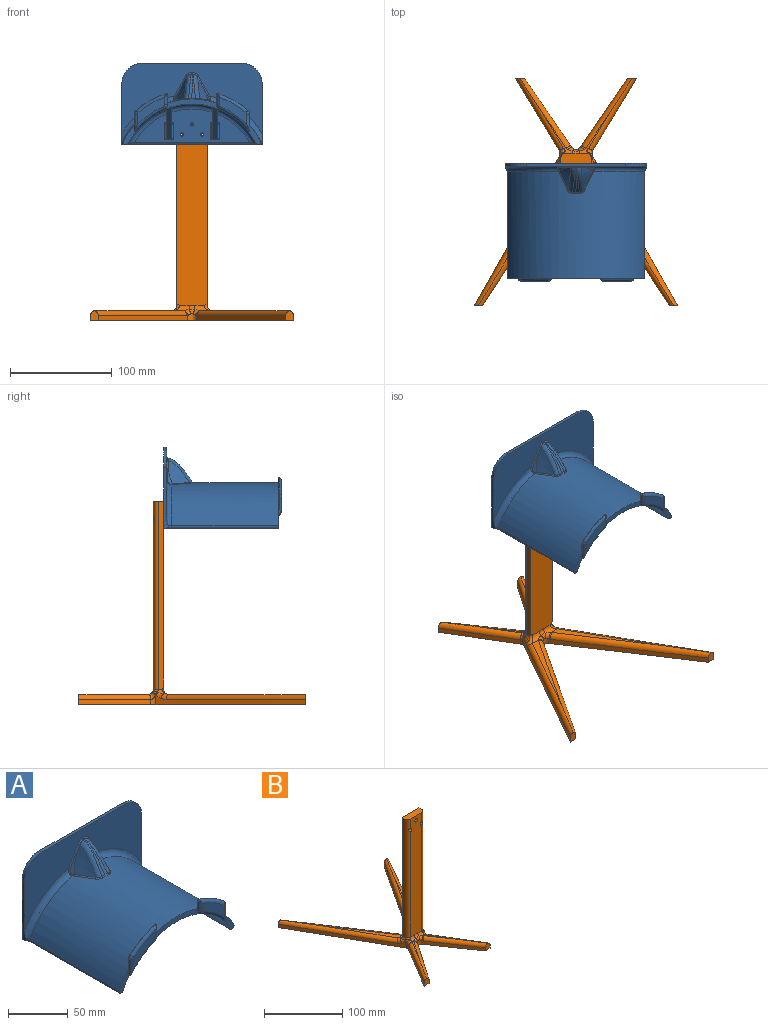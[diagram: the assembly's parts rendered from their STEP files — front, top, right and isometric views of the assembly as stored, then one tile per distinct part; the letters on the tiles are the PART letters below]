
ASSEMBLY  parts=2 mates=1
PART A: 117 faces, bbox 168.4x120.5x87.3 mm
  f0: plane 113.62x33mm, normal (0,-1,0), area 2335.8mm2, adj f27,f31,f46,f47,f52,f53,f54,f55
  f1: cylinder r=75.4mm len=135.31mm, axis (0,1,0), area 17098.7mm2, adj f3,f5,f8,f12,f14,f21,f22,f26
  f2: plane 138x69.13mm, normal (0,-1,0), area 5103.2mm2, adj f3,f9,f10,f28,f38,f40,f42,f44
  f3: torus R=80.4mm, axis (0,1,0), area 521.9mm2, adj f1,f2,f9,f32,f45
  f4: bspline ~27.73x26.84mm, area 286.1mm2, adj f35,f36,f41,f42
  f5: plane 19.26x12.92mm, normal (0,-1,0), area 88.7mm2, adj f1,f6,f7,f14,f15,f29,f33
  f6: plane 138.01x113mm, normal (0,0,-1), area 431mm2, adj f5,f9,f11,f29,f30,f31,f32,f33
  f7: cylinder r=70.4mm len=125.91mm, axis (0,1,0), area 15710.7mm2, adj f5,f8,f17,f27,f29,f56,f57,f58
  f8: plane 54.51x10.49mm, normal (0,-1,0), area 250.7mm2, adj f1,f7,f19,f21,f95,f97
  f9: plane 60.93x5.96mm, normal (-1,0,0), area 189mm2, adj f2,f3,f6,f11,f28,f32
  f10: plane 98x3mm, normal (0,0,1), area 294mm2, adj f2,f11,f28,f89
  f11: plane 138x80mm, normal (0,1,0), area 10844.2mm2, adj f6,f9,f10,f28,f46,f47,f72,f89
  f12: plane 31.56x30.04mm, normal (0,1,0), area 324.4mm2, adj f1,f22,f23,f24,f25,f26
  f13: plane 27.11x26.66mm, normal (0,-1,0), area 261.6mm2, adj f14,f16,f17,f18,f19,f21
  f14: cylinder r=3mm len=15.97mm, axis (0,0,1), area 59.3mm2, adj f1,f5,f13,f15,f16,f26
  f15: bspline ~8.26x3.25mm, area 7.4mm2, adj f5,f14,f17
  f16: torus R=2mm, axis (0,-1,0), area 13.3mm2, adj f13,f14,f18,f25
  f17: torus R=73.4mm, axis (0,-1,0), area 156mm2, adj f7,f13,f15,f19
  f18: torus R=81.64mm, axis (0,-1,0), area 132.3mm2, adj f13,f16,f20,f24
  f19: torus R=2mm, axis (0,-1,0), area 21.6mm2, adj f8,f13,f17,f21
  f20: bspline ~4.11x2.99mm, area 3.5mm2, adj f18,f21,f23
  f21: cylinder r=3mm len=10.19mm, axis (0,0,-1), area 38.5mm2, adj f1,f8,f13,f19,f20,f22
  f22: cylinder r=0.5mm len=8.48mm, axis (0,0,-1), area 7.4mm2, adj f1,f12,f21,f23
  f23: bspline ~1.67x1.4mm, area 1.4mm2, adj f12,f20,f22,f24
  f24: torus R=84.09mm, axis (0,-1,0), area 30.1mm2, adj f12,f18,f23,f25
  f25: torus R=4.45mm, axis (0,-1,0), area 3.7mm2, adj f12,f16,f24,f26
  f26: cylinder r=0.5mm len=10.86mm, axis (0,0,1), area 9.4mm2, adj f1,f12,f14,f25
  f27: torus R=65.4mm, axis (0,1,0), area 1163.5mm2, adj f0,f7,f30,f87
  f28: cylinder r=20mm len=20mm, axis (0,1,0), area 94.2mm2, adj f2,f9,f10,f11
  f29: cylinder r=2mm len=105mm, axis (0,1,0), area 232.4mm2, adj f5,f6,f7,f30
  f30: bspline ~9.13x8.44mm, area 25.7mm2, adj f6,f27,f29,f31
  f31: cylinder r=2mm len=113.62mm, axis (-1,0,0), area 356.9mm2, adj f0,f6,f30,f87
  f32: bspline ~7.84x5.46mm, area 18.1mm2, adj f3,f6,f9,f33
  f33: cylinder r=2mm len=105mm, axis (0,1,0), area 425.9mm2, adj f1,f5,f6,f32
  f34: bspline ~27.73x26.84mm, area 69.9mm2, adj f35,f37,f38,f84
  f35: bspline ~28.07x27.3mm, area 174.2mm2, adj f4,f34,f39,f40
  f36: plane 20.23x12.7mm, normal (-0.81,-0.36,0.47), area 40.1mm2, adj f4,f41,f42,f43,f44,f45
  f37: bspline ~5.9x1.33mm, area 4.9mm2, adj f1,f34,f39,f81
  f38: bspline ~2.95x1.49mm, area 1.9mm2, adj f2,f34,f40,f80
  f39: bspline ~7.03x4.77mm, area 8.9mm2, adj f1,f35,f37,f41
  f40: bspline ~7.59x4.87mm, area 13.5mm2, adj f2,f35,f38,f42
  f41: bspline ~25.84x13.27mm, area 28.8mm2, adj f1,f4,f36,f39,f43
  f42: bspline ~16.15x9.28mm, area 18.5mm2, adj f2,f4,f36,f40,f44
  f43: bspline ~1.94x1.59mm, area 2.1mm2, adj f1,f36,f41,f45
  f44: cylinder r=1.5mm len=12.64mm, axis (0.5,0,0.86), area 24.8mm2, adj f2,f36,f42,f45
  f45: bspline ~5.54x5.34mm, area 9.6mm2, adj f3,f36,f43,f44
  f46: cylinder r=1.6mm len=3.2mm, axis (0,-1,0), area 30.2mm2, adj f0,f11
  f47: cylinder r=1.6mm len=3.2mm, axis (0,-1,0), area 30.2mm2, adj f0,f11
  f48: plane 71.79x30.75mm, normal (0,-0.39,-0.92), area 379.7mm2, adj f50,f51,f53,f54,f55,f56,f58,f59
  f49: plane 38.31x13.53mm, normal (0,0.33,0.94), area 190.6mm2, adj f50,f51,f52,f57
  f50: plane 67.76x29.12mm, normal (1,0,0), area 596.8mm2, adj f48,f49,f52,f53,f57,f59
  f51: plane 60.01x25.61mm, normal (-1,0,0), area 522.8mm2, adj f48,f49,f52,f54,f56,f57
  f52: cylinder r=2mm len=9mm, axis (1,0,0), area 23.7mm2, adj f0,f49,f50,f51,f53,f54
  f53: cylinder r=2mm len=16.73mm, axis (0,0,-1), area 45.6mm2, adj f0,f48,f50,f52,f55
  f54: cylinder r=2mm len=16.73mm, axis (0,0,1), area 45.6mm2, adj f0,f48,f51,f52,f55
  f55: cylinder r=2mm len=9mm, axis (-1,0,0), area 16.7mm2, adj f0,f48,f53,f54
  f56: cylinder r=2mm len=33.98mm, axis (0,1,0), area 113.6mm2, adj f7,f48,f51,f57,f58
  f57: bspline ~24.07x21.1mm, area 45.7mm2, adj f7,f49,f50,f51,f56,f59
  f58: bspline ~9.79x8.16mm, area 11.6mm2, adj f7,f48,f56,f59
  f59: cylinder r=2mm len=32.46mm, axis (0,1,0), area 77.1mm2, adj f7,f48,f50,f57,f58
  f60: cylinder r=2mm len=32.46mm, axis (0,1,0), area 77.1mm2, adj f7,f61,f62,f69,f71
  f61: bspline ~9.79x8.16mm, area 11.6mm2, adj f7,f60,f63,f71
  f62: bspline ~24.07x21.1mm, area 45.7mm2, adj f7,f60,f63,f68,f69,f70
  f63: cylinder r=2mm len=33.98mm, axis (0,1,0), area 113.6mm2, adj f7,f61,f62,f68,f71
  f64: cylinder r=2mm len=9mm, axis (1,0,0), area 16.7mm2, adj f0,f65,f66,f71
  f65: cylinder r=2mm len=16.73mm, axis (0,0,1), area 45.6mm2, adj f0,f64,f67,f68,f71
  f66: cylinder r=2mm len=16.73mm, axis (0,0,-1), area 45.6mm2, adj f0,f64,f67,f69,f71
  f67: cylinder r=2mm len=9mm, axis (-1,0,0), area 23.7mm2, adj f0,f65,f66,f68,f69,f70
  f68: plane 60.01x25.61mm, normal (1,0,0), area 522.8mm2, adj f62,f63,f65,f67,f70,f71
  f69: plane 67.76x29.12mm, normal (-1,0,0), area 596.8mm2, adj f60,f62,f66,f67,f70,f71
  f70: plane 38.31x13.53mm, normal (0,0.33,0.94), area 190.6mm2, adj f62,f67,f68,f69
  f71: plane 71.79x30.75mm, normal (0,-0.39,-0.92), area 379.7mm2, adj f60,f61,f63,f64,f65,f66,f68,f69
  f72: cylinder r=1.6mm len=3.2mm, axis (0,-1,0), area 30.2mm2, adj f0,f11
  f73: bspline ~5.54x5.34mm, area 9.6mm2, adj f74,f75,f82,f108
  f74: cylinder r=1.5mm len=12.64mm, axis (-0.5,0,0.86), area 24.8mm2, adj f2,f73,f76,f82
  f75: bspline ~1.94x1.59mm, area 2.1mm2, adj f1,f73,f77,f82
  f76: bspline ~16.15x9.28mm, area 18.5mm2, adj f2,f74,f78,f82,f107
  f77: bspline ~25.84x13.27mm, area 28.8mm2, adj f1,f75,f79,f82,f107
  f78: bspline ~7.59x4.87mm, area 13.5mm2, adj f2,f76,f80,f83
  f79: bspline ~7.27x5.49mm, area 8.9mm2, adj f1,f77,f81,f83
  f80: bspline ~2.95x1.49mm, area 1.9mm2, adj f2,f38,f78,f84
  f81: bspline ~5.9x1.33mm, area 4.9mm2, adj f1,f37,f79,f84
  f82: plane 20.23x12.7mm, normal (0.81,-0.36,0.47), area 40.1mm2, adj f73,f74,f75,f76,f77,f107
  f83: bspline ~28.07x27.3mm, area 174.2mm2, adj f78,f79,f84,f107
  f84: bspline ~27.73x26.84mm, area 69.9mm2, adj f34,f80,f81,f83
  f85: cylinder r=2mm len=105mm, axis (0,1,0), area 425.9mm2, adj f1,f6,f86,f106
  f86: bspline ~7.84x5.46mm, area 18.1mm2, adj f6,f85,f105,f108
  f87: bspline ~9.13x8.44mm, area 25.7mm2, adj f6,f27,f31,f88
  f88: cylinder r=2mm len=105mm, axis (0,1,0), area 232.4mm2, adj f6,f7,f87,f106
  f89: cylinder r=20mm len=20mm, axis (0,1,0), area 94.2mm2, adj f2,f10,f11,f105
  f90: cylinder r=0.5mm len=10.86mm, axis (0,0,1), area 9.4mm2, adj f1,f91,f102,f104
  f91: torus R=4.45mm, axis (0,-1,0), area 3.7mm2, adj f90,f92,f100,f104
  f92: torus R=84.09mm, axis (0,-1,0), area 30.1mm2, adj f91,f93,f98,f104
  f93: bspline ~1.67x1.4mm, area 1.4mm2, adj f92,f94,f96,f104
  f94: cylinder r=0.5mm len=8.48mm, axis (0,0,-1), area 7.4mm2, adj f1,f93,f95,f104
  f95: cylinder r=3mm len=10.19mm, axis (0,0,-1), area 38.5mm2, adj f1,f8,f94,f96,f97,f103
  f96: bspline ~4.11x2.99mm, area 3.5mm2, adj f93,f95,f98
  f97: torus R=2mm, axis (0,-1,0), area 21.6mm2, adj f8,f95,f99,f103
  f98: torus R=81.64mm, axis (0,-1,0), area 132.3mm2, adj f92,f96,f100,f103
  f99: torus R=73.4mm, axis (0,-1,0), area 156mm2, adj f7,f97,f101,f103
  f100: torus R=2mm, axis (0,-1,0), area 13.3mm2, adj f91,f98,f102,f103
  f101: bspline ~8.26x3.25mm, area 7.4mm2, adj f99,f102,f106
  f102: cylinder r=3mm len=15.97mm, axis (0,0,1), area 59.3mm2, adj f1,f90,f100,f101,f103,f106
  f103: plane 27.11x26.66mm, normal (0,-1,0), area 261.6mm2, adj f95,f97,f98,f99,f100,f102
  f104: plane 31.56x30.04mm, normal (0,1,0), area 324.4mm2, adj f1,f90,f91,f92,f93,f94
  f105: plane 60.93x5.96mm, normal (1,0,0), area 189mm2, adj f2,f6,f11,f86,f89,f108
  f106: plane 19.26x12.92mm, normal (0,-1,0), area 88.7mm2, adj f1,f6,f7,f85,f88,f101,f102
  f107: bspline ~27.73x26.84mm, area 286.1mm2, adj f76,f77,f82,f83
  f108: torus R=80.4mm, axis (0,1,0), area 521.9mm2, adj f1,f2,f73,f86,f105
  f109: bspline ~15.81x11.41mm, area 33.8mm2, adj f110,f111,f114,f115,f116
  f110: bspline ~15.81x5.67mm, area 2.1mm2, adj f109,f111,f114
  f111: plane 2.42x2.39mm, normal (-0.81,0.36,-0.47), area 1mm2, adj f109,f110,f114
  f112: bspline ~15.81x5.67mm, area 2.1mm2, adj f113,f114,f115
  f113: plane 2.42x2.39mm, normal (0.81,0.36,-0.47), area 1mm2, adj f112,f114,f115
  f114: torus R=80.4mm, axis (0,1,0), area 65.8mm2, adj f109,f110,f111,f112,f113,f115,f116
  f115: bspline ~15.81x11.41mm, area 33.8mm2, adj f109,f112,f113,f114,f116
  f116: cylinder r=75.4mm len=5.47mm, axis (0,1,0), area 2.7mm2, adj f109,f114,f115
PART B: 77 faces, bbox 201.1x230.3x201.1 mm
  f0: cylinder r=1mm len=5mm, axis (0,1,0), area 31.4mm2, adj f6,f71
  f1: cylinder r=1mm len=5mm, axis (0,1,0), area 31.4mm2, adj f6,f75
  f2: cylinder r=1mm len=5mm, axis (0,1,0), area 31.4mm2, adj f6,f73
  f3: plane 33.21x22.68mm, normal (0,0,1), area 44.9mm2, adj f36,f66,f68,f70
  f4: plane 93.77x61.62mm, normal (0,0,1), area 397.8mm2, adj f29,f37,f39
  f5: plane 33.21x22.68mm, normal (0,0,1), area 44.9mm2, adj f33,f53,f55,f58
  f6: plane 185.34x30.26mm, normal (0,1,0), area 5533.6mm2, adj f0,f1,f2,f7,f8,f17,f29,f30
  f7: plane 185.41x5.41mm, normal (1,0,0), area 923.5mm2, adj f6,f8,f34,f54,f56
  f8: plane 30x10mm, normal (0,0,1), area 289.3mm2, adj f6,f7,f10,f17,f44,f56
  f9: plane 224.08x200mm, normal (0,0,-1), area 6174.2mm2, adj f11,f12,f13,f14,f15,f16,f18,f19
  f10: plane 185.13x20mm, normal (0,-1,0), area 3661.2mm2, adj f8,f33,f35,f36,f44,f56,f72,f74
  f11: plane 133.64x87.82mm, normal (-0.84,0.55,0), area 799.6mm2, adj f9,f12,f28,f48,f50
  f12: plane 10.75x9.01mm, normal (0,1,0), area 67.7mm2, adj f9,f11,f13,f50,f52
  f13: plane 147.67x83.77mm, normal (0.87,-0.49,0), area 864.1mm2, adj f9,f12,f27,f52,f54,f57
  f14: plane 71.58x43.07mm, normal (0.86,0.52,0), area 417.7mm2, adj f9,f15,f27,f68
  f15: plane 10.99x10.12mm, normal (0,-1,0), area 77.1mm2, adj f9,f14,f16,f68,f70
  f16: plane 68.04x46.48mm, normal (-0.83,-0.56,0), area 412.1mm2, adj f9,f15,f26,f69,f70
  f17: plane 185.41x5.41mm, normal (-1,0,0), area 923.5mm2, adj f6,f8,f31,f41,f44
  f18: plane 133.64x87.82mm, normal (0.84,0.55,0), area 799.6mm2, adj f9,f19,f28,f37,f38
  f19: plane 10.75x9.01mm, normal (0,1,0), area 67.7mm2, adj f9,f18,f20,f37,f39
  f20: plane 147.67x83.77mm, normal (-0.87,-0.49,0), area 864.1mm2, adj f9,f19,f25,f39,f41,f43
  f21: plane 93.77x61.62mm, normal (0,0,1), area 397.8mm2, adj f32,f50,f52
  f22: plane 71.58x43.07mm, normal (-0.86,0.52,0), area 417.7mm2, adj f9,f23,f25,f55
  f23: plane 10.99x10.12mm, normal (0,-1,0), area 77.1mm2, adj f9,f22,f24,f55,f58
  f24: plane 68.04x46.48mm, normal (0.83,-0.56,0), area 412.1mm2, adj f9,f23,f26,f58,f61
  f25: cylinder r=5mm len=9.86mm, axis (0,0,-1), area 36.1mm2, adj f9,f20,f22,f46,f51,f53
  f26: cylinder r=5mm len=8.26mm, axis (0,0,1), area 60.3mm2, adj f9,f16,f24,f63,f65,f67
  f27: cylinder r=5mm len=9.86mm, axis (0,0,-1), area 36.1mm2, adj f9,f13,f14,f60,f64,f66
  f28: cylinder r=5mm len=8.36mm, axis (0,0,1), area 60.3mm2, adj f9,f11,f18,f40,f42,f45
  f29: cylinder r=5mm len=14.9mm, axis (1,0,0), area 78.5mm2, adj f4,f6,f30,f38,f40,f41
  f30: bspline ~7.91x5.82mm, area 26.1mm2, adj f6,f29,f32,f42
  f31: cylinder r=5mm len=6.71mm, axis (0,1,0), area 21.8mm2, adj f17,f41,f43,f46,f47
  f32: cylinder r=5mm len=14.9mm, axis (-1,0,0), area 78.5mm2, adj f6,f21,f30,f45,f48,f54
  f33: cylinder r=5mm len=9mm, axis (1,0,0), area 51mm2, adj f5,f10,f35,f47,f51,f61,f63
  f34: cylinder r=5mm len=6.71mm, axis (0,1,0), area 21.8mm2, adj f7,f54,f57,f59,f60
  f35: bspline ~7.63x5.34mm, area 27.9mm2, adj f10,f33,f36,f65
  f36: cylinder r=5mm len=9mm, axis (-1,0,0), area 51mm2, adj f3,f10,f35,f59,f64,f67,f69
  f37: cylinder r=5mm len=136.87mm, axis (0.55,-0.84,0), area 1214.5mm2, adj f4,f18,f19,f38,f39
  f38: bspline ~5.09x5.05mm, area 9.9mm2, adj f18,f29,f37,f40
  f39: cylinder r=5mm len=139.93mm, axis (-0.49,0.87,0), area 1192.7mm2, adj f4,f19,f20,f37,f41
  f40: bspline ~8.67x5.95mm, area 26.9mm2, adj f28,f29,f38,f42
  f41: bspline ~15.24x12.46mm, area 63.2mm2, adj f6,f17,f20,f29,f31,f39,f43
  f42: bspline ~6.13x4.28mm, area 20.2mm2, adj f28,f30,f40,f45
  f43: bspline ~7.74x5.65mm, area 27.6mm2, adj f20,f31,f41,f46
  f44: cylinder r=5mm len=185mm, axis (0,0,-1), area 1442.8mm2, adj f8,f10,f17,f47,f74
  f45: bspline ~7.97x5.87mm, area 26.9mm2, adj f28,f32,f42,f48
  f46: bspline ~4.46x4.42mm, area 4.7mm2, adj f25,f31,f43,f49
  f47: bspline ~5.71x5.71mm, area 17.9mm2, adj f31,f33,f44,f49
  f48: bspline ~5.09x5.05mm, area 9.9mm2, adj f11,f32,f45,f50
  f49: sphere r=5mm, area 9.8mm2, adj f46,f47,f51
  f50: cylinder r=5mm len=136.87mm, axis (-0.55,-0.84,0), area 1214.5mm2, adj f11,f12,f21,f48,f52
  f51: bspline ~8.29x7.5mm, area 37.7mm2, adj f25,f33,f49,f53
  f52: cylinder r=5mm len=139.93mm, axis (0.49,0.87,0), area 1192.7mm2, adj f12,f13,f21,f50,f54
  f53: torus R=10mm, axis (0,0,-1), area 0.5mm2, adj f5,f25,f51,f55
  f54: bspline ~15.24x12.46mm, area 63.2mm2, adj f6,f7,f13,f32,f34,f52,f57
  f55: cylinder r=5mm len=74.16mm, axis (0.52,0.86,0), area 619.4mm2, adj f5,f22,f23,f53,f58
  f56: cylinder r=5mm len=185mm, axis (0,0,-1), area 1442.8mm2, adj f7,f8,f10,f59,f72
  f57: bspline ~7.74x5.65mm, area 27.6mm2, adj f13,f34,f54,f60
  f58: cylinder r=5mm len=71.21mm, axis (-0.56,-0.83,0), area 615.5mm2, adj f5,f23,f24,f55,f61
  f59: bspline ~5.71x5.71mm, area 17.9mm2, adj f34,f36,f56,f62
  f60: bspline ~4.46x4.42mm, area 4.7mm2, adj f27,f34,f57,f62
  f61: bspline ~7.37x6.06mm, area 12.9mm2, adj f24,f33,f58,f63
  f62: sphere r=5mm, area 13.4mm2, adj f59,f60,f64
  f63: bspline ~8.41x6.02mm, area 24.8mm2, adj f26,f33,f61,f65
  f64: bspline ~8.35x8.08mm, area 37.7mm2, adj f27,f36,f62,f66
  f65: bspline ~6.35x4.19mm, area 21.9mm2, adj f26,f35,f63,f67
  f66: torus R=10mm, axis (0,0,-1), area 0.5mm2, adj f3,f27,f64,f68
  f67: bspline ~8.41x6.02mm, area 24.8mm2, adj f26,f36,f65,f69
  f68: cylinder r=5mm len=74.16mm, axis (-0.52,0.86,0), area 619.4mm2, adj f3,f14,f15,f66,f70
  f69: bspline ~7.37x6.06mm, area 12.9mm2, adj f16,f36,f67,f70
  f70: cylinder r=5mm len=71.21mm, axis (0.56,-0.83,0), area 615.5mm2, adj f3,f15,f16,f68,f69
  f71: plane 5x5mm, normal (0,-1,0), area 16.5mm2, adj f0,f72
  f72: cylinder r=2.5mm len=5mm, axis (0,-1,0), area 78.5mm2, adj f10,f56,f71
  f73: plane 5x5mm, normal (0,-1,0), area 16.5mm2, adj f2,f74
  f74: cylinder r=2.5mm len=5mm, axis (0,-1,0), area 78.5mm2, adj f10,f44,f73
  f75: plane 5x5mm, normal (0,-1,0), area 16.5mm2, adj f1,f76
  f76: cylinder r=2.5mm len=5mm, axis (0,-1,0), area 78.5mm2, adj f10,f75
PLACE A t=(-71.6,27.28,-19.78)mm
PLACE B rot(axis=(0,0,1),180deg) t=(-86.6,30.28,-134.09)mm
MATE fastened B.f1 <-> A.f46  axis (0,-1,0) through (-71.6,30.28,0.22)mm
